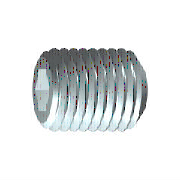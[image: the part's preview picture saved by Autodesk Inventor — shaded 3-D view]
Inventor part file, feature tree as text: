
AUTODESK INVENTOR PART (.ipt)
format: ipt  version: 2017 (Build 210142000, 142)  size: 163,840 bytes
history: native  units: mm (DEFAULTED — no unit token found)
features: sketch x2, extrude x1, other x1, plane x1
ambient origin geometry x8: Origin, YZ Plane, XZ Plane, XY Plane, X Axis, Y Axis, Z Axis, Center Point
bodies: Solid1 (feature_tree), Body (feature_tree)
feature tree (5):
  extrude  "Slot"  TaperAngle=60.0deg  [1 undecoded]
  other  "Work Axis1"
  plane  "Work Plane1"
  sketch  "Sketch1"  dims[d0=2.1mm d1=60.0deg]
  sketch  "Sketch2"  dims[d2=3.0mm d3=1.732051mm d6=90.0deg d4=0.0mm d5=5.0mm d7=0.306725mm d8=45.0deg d21=10.0mm d9=0.0mm d11=5.0mm d12=0.0mm d13=0.306725mm d14=45.0deg d15=0.0mm d29=0.306725mm d30=0.306725mm d31=0.0mm]
note: 1 required parameter value undecoded (feature->parameter linkage not recoverable at this tier; creation-order binding heuristic only, values carry confidence <= 0.55)
